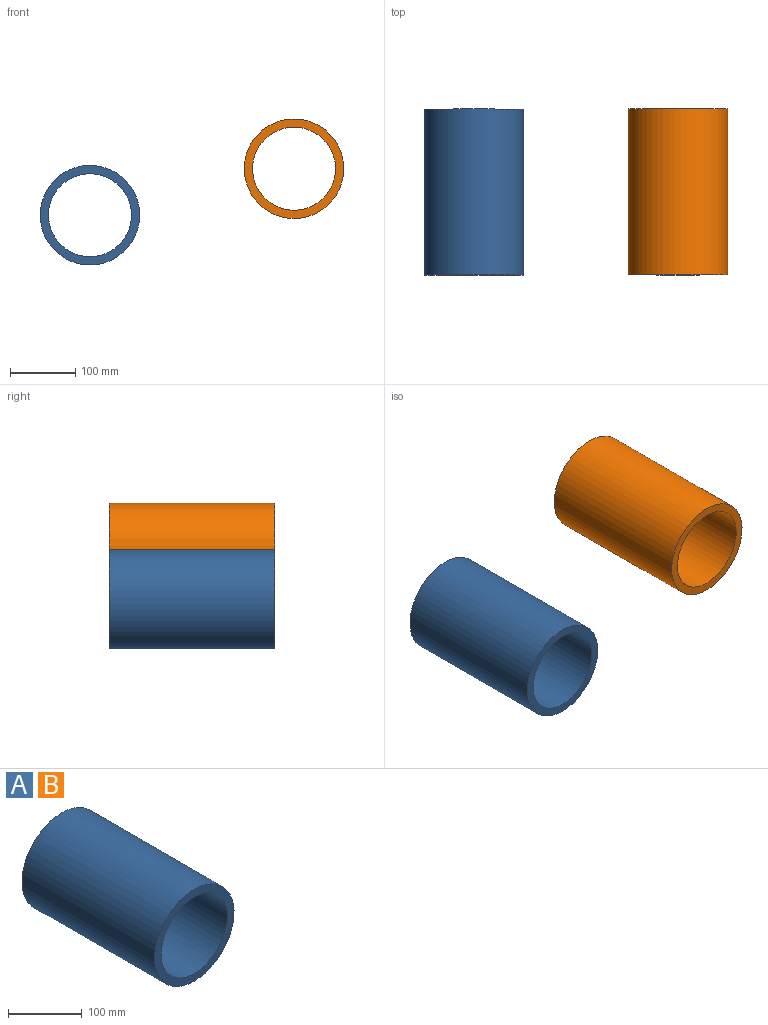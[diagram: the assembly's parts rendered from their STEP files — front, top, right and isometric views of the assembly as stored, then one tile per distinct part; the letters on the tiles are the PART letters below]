
ASSEMBLY  parts=2 mates=1
PART A: 4 faces, bbox 152.4x254x152.4 mm
  f0: cylinder r=63.5mm len=254mm, axis (0,1,0), area 101341.5mm2, adj f2,f3
  f1: cylinder r=76.2mm len=254mm, axis (0,1,0), area 121609.8mm2, adj f2,f3
  f2: plane 152.4x152.4mm, normal (0,-1,0), area 5573.8mm2, adj f0,f1
  f3: plane 152.4x152.4mm, normal (0,1,0), area 5573.8mm2, adj f0,f1
PART B: same geometry as A
PLACE A rot(axis=(0,-1,0),7deg) t=(-219.27,-177.02,-258.01)mm
PLACE B t=(93.15,-177.02,-186.89)mm
MATE parallel B.f1 <-> A.f1  axis (0,1,0) through (93.15,-177.02,-186.89)mm
